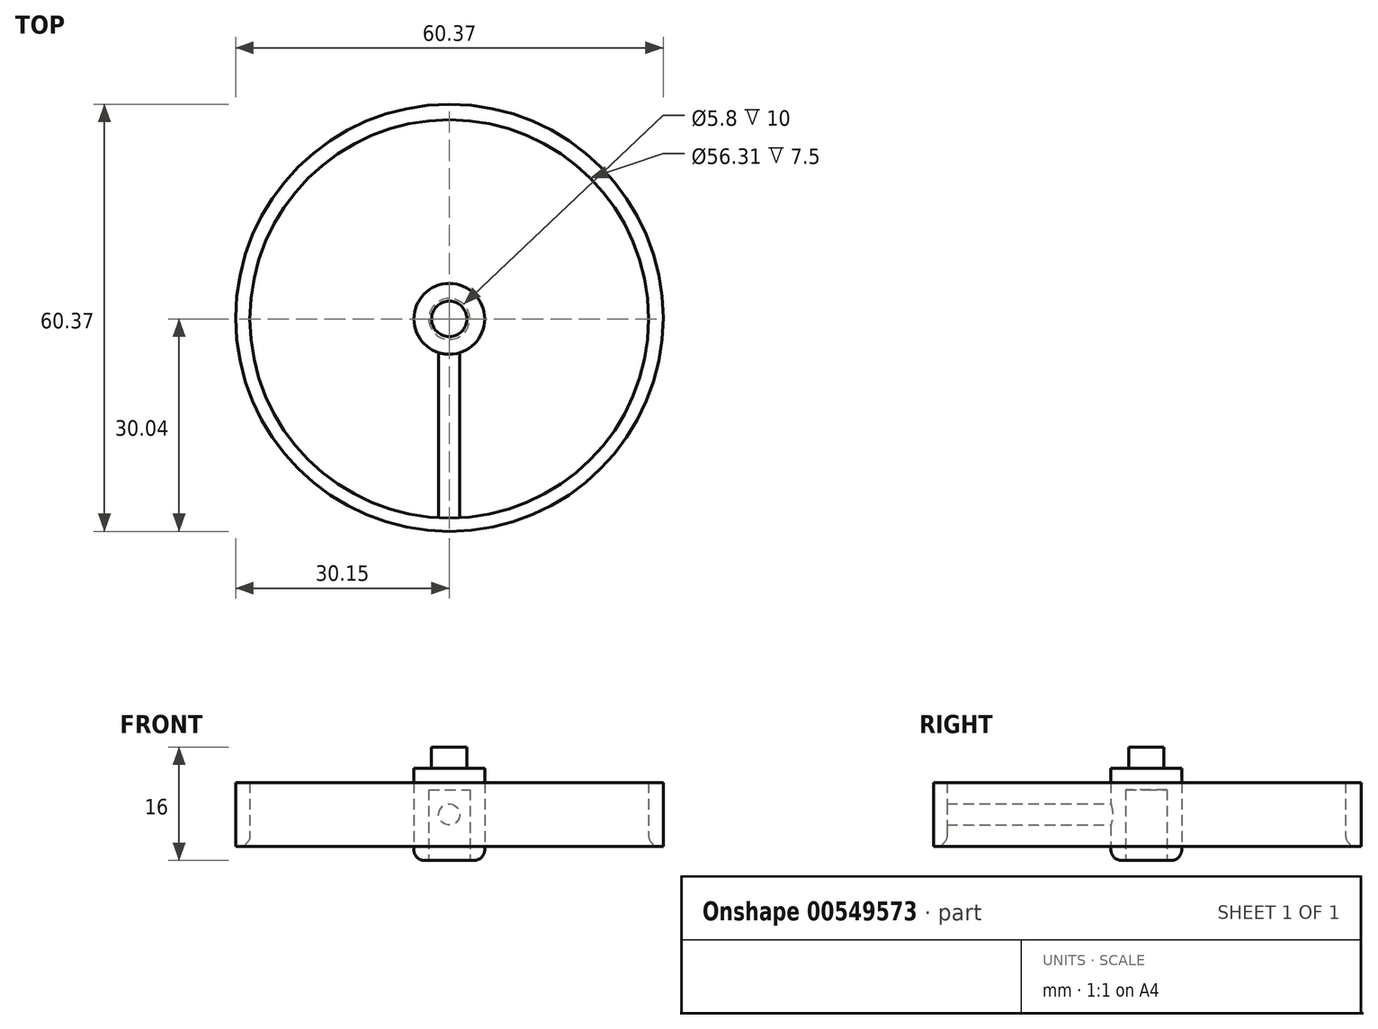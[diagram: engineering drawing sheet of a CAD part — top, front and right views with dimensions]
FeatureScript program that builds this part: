
annotation { "Feature Type Name" : "Feature", "Feature Type Description" : "" }
export const myFeature = defineFeature(function(context is Context, id is Id, definition is map)
    precondition{}
    {
        {
            var Q0;
            Q0=qCreatedBy(makeId("Top.planeOp"),FACE);
            var sketch = newSketch(context, id + "F0", { "sketchPlane" : qUnion([Q0])});
            skCircle(sketch, "E0", {"center": v(0, 0) * mm, "radius": 5 * mm});
            skSolve(sketch);
        }
        {
            var Q0;
            Q0=qSketchRegion(id+"F0",true);
            extrude(context, id + "F1", {"entities" : qUnion([Q0]), "endBound" : BoundingType.SYMMETRIC, "depth" : 13 * mm, "offsetDistance" : 25 * mm});
        }
        {
            var Q0;
            Q0=makeQuery(id+"F1.opExtrude","CAP_FACE",FACE,{"disambiguationData":[OSD([sQuery(id+"F0.wireOp",EDGE,"E0")])],"isStart":true});
            var sketch = newSketch(context, id + "F2", { "sketchPlane" : qUnion([Q0])});
            skCircle(sketch, "E1", {"center": v(0, 0) * mm, "radius": 2.9 * mm});
            skSolve(sketch);
        }
        {
            var Q0;
            Q0=qSketchRegion(id+"F2",true);
            extrude(context, id + "F3", {"entities" : qUnion([Q0]), "operationType" : NewBodyOperationType.REMOVE, "oppositeDirection" : true, "depth" : 10 * mm, "offsetDistance" : 25 * mm});
        }
        {
            var Q0;
            Q0=qCreatedBy(makeId("Top.planeOp"),FACE);
            var sketch = newSketch(context, id + "F4", { "sketchPlane" : qUnion([Q0])});
            skLineSegment(sketch, "E2", {"start": v(0, 0) * mm, "end": v(0, -46.52) * mm, "construction": true});
            skLineSegment(sketch, "E3", {"start": v(0, -4.77) * mm, "end": v(-1.5, -4.77) * mm});
            skLineSegment(sketch, "E4", {"start": v(-1.5, -4.77) * mm, "end": v(-1.5, -30) * mm});
            skLineSegment(sketch, "E5", {"start": v(0, -4.77) * mm, "end": v(0, -30) * mm});
            skLineSegment(sketch, "E6", {"start": v(0, -30) * mm, "end": v(-1.5, -30) * mm});
            skSolve(sketch);
        }
        {
            var Q0;
            Q0=qSketchRegion(id+"F4",true);
            var Q1;
            Q1=sQuery(id+"F4.wireOp",EDGE,"E2");
            revolve(context, id + "F5", {"operationType" : NewBodyOperationType.ADD, "entities" : qUnion([Q0]), "axis" : qUnion([Q1]), "revolveType" : RevolveType.FULL});
        }
        {
            var Q0;
            Q0=qCreatedBy(makeId("Top.planeOp"),FACE);
            var sketch = newSketch(context, id + "F6", { "sketchPlane" : qUnion([Q0])});
            skCircle(sketch, "E7", {"center": v(0.03, 0.15) * mm, "radius": 30.18 * mm});
            skCircle(sketch, "E8", {"center": v(0, 0) * mm, "radius": 28.15 * mm});
            skLineSegment(sketch, "E9", {"start": v(-28.15, 0.15) * mm, "end": v(-30.15, 0.15) * mm, "construction": true});
            skSolve(sketch);
        }
        {
            var Q0;
            Q0 = qSketchRegion(id + "F6", true);
            extrude(context, id + "F7", {"entities" : qUnion([Q0]), "operationType" : NewBodyOperationType.ADD, "endBound" : BoundingType.SYMMETRIC, "depth" : 9 * mm, "offsetDistance" : 25 * mm});
        }
        {
            var Q0;
            Q0=makeQuery(id+"F1.opExtrude","CAP_EDGE",EDGE,{"disambiguationData":[OSD([sQuery(id+"F0.wireOp",EDGE,"E0")])],"isStart":true});
            var Q1;
            Q1=makeQuery(id+"F7.opExtrude","CAP_EDGE",EDGE,{"disambiguationData":[OSD([sQuery(id+"F6.wireOp",EDGE,"E8")])],"isStart":true});
            fillet(context, id + "F8", {"entities" : qUnion([Q0, Q1]), "radius" : 1.5 * mm, "tangentPropagation" : true, "allowEdgeOverflow" : false});
        }
        {
            var Q0;
            Q0=makeQuery(id+"F1.opExtrude","CAP_FACE",FACE,{"disambiguationData":[OSD([sQuery(id+"F0.wireOp",EDGE,"E0")])],"isStart":false});
            var sketch = newSketch(context, id + "F9", { "sketchPlane" : qUnion([Q0])});
            skCircle(sketch, "E10", {"center": v(0, 0) * mm, "radius": 2.5 * mm});
            skSolve(sketch);
        }
        {
            var Q0;
            Q0 = qSketchRegion(id + "F9", true);
            extrude(context, id + "F10", {"entities" : qUnion([Q0]), "operationType" : NewBodyOperationType.ADD, "depth" : 3 * mm, "offsetDistance" : 25 * mm});
        }
    });
